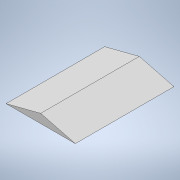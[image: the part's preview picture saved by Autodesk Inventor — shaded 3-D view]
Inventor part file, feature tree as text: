
AUTODESK INVENTOR PART (.ipt)
format: ipt  version: 2022.1 (Build 261234000, 234)  size: 92,672 bytes
history: native  units: in
note: dims shown in document units (in); Inventor stores cm internally (conversion verified against a paired STEP export)
features: extrude x1, sketch x1
ambient origin geometry x8: Origin, YZ Plane, XZ Plane, XY Plane, X Axis, Y Axis, Z Axis, Center Point
bodies: Solid1 (feature_tree)
feature tree (2):
  extrude  "Extrusion1"  Depth=768.0in
  sketch  "Sketch1"  dims[d0=0.0992in d1=0.0992in d2=278.5in d3=278.5in d4=768.0in d5=0.0in]
